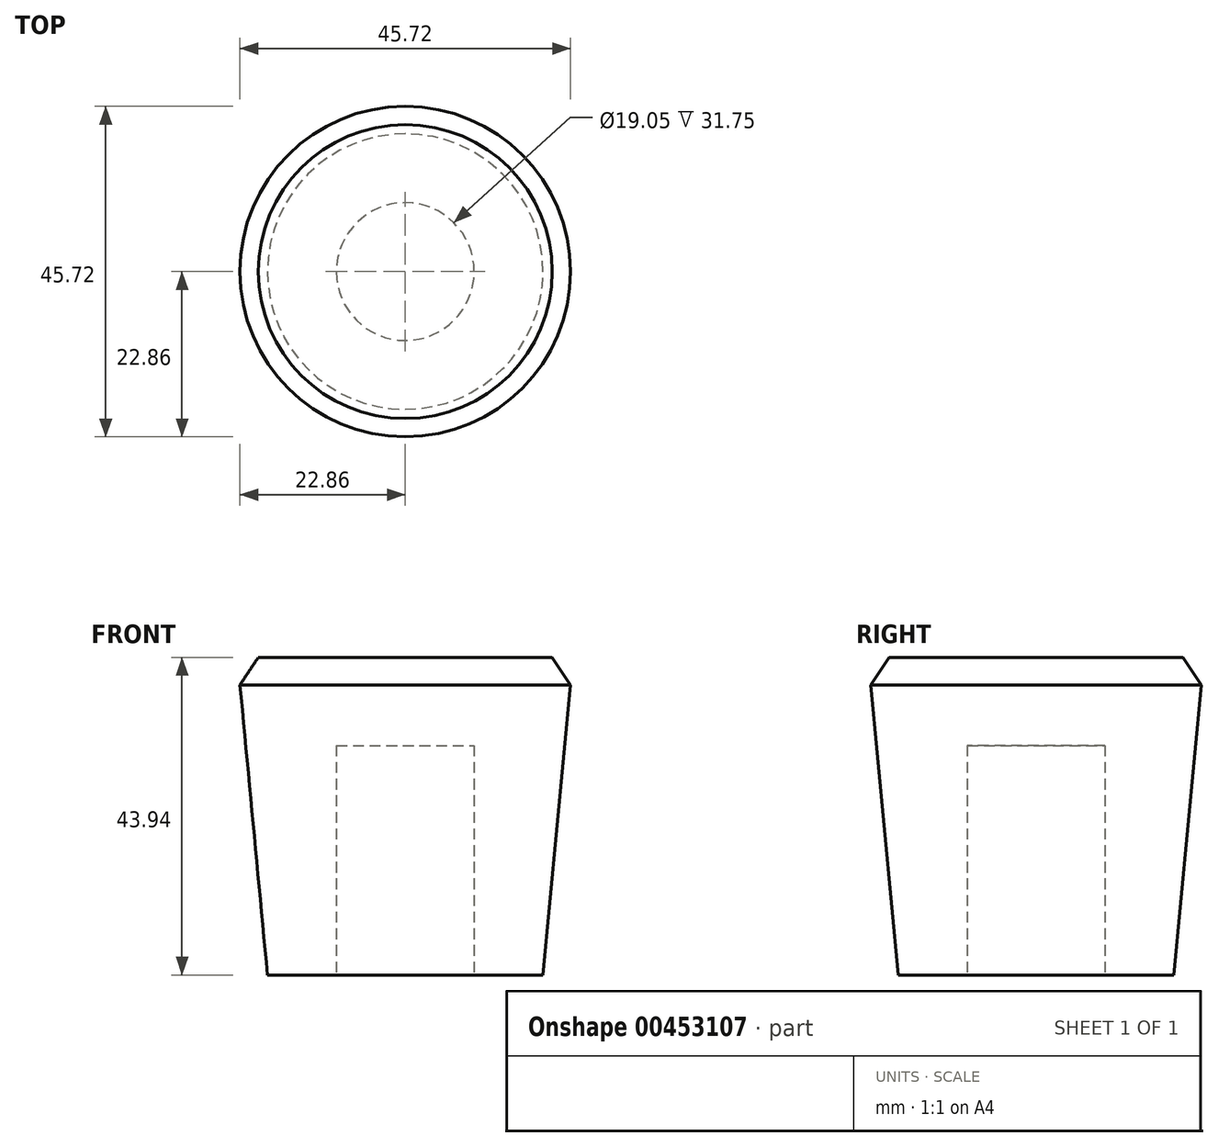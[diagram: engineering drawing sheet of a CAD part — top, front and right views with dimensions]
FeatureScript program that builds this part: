
annotation { "Feature Type Name" : "Feature", "Feature Type Description" : "" }
export const myFeature = defineFeature(function(context is Context, id is Id, definition is map)
    precondition{}
    {
        {
            var Q0;
            Q0=qCreatedBy(makeId("Front.planeOp"),FACE);
            var sketch = newSketch(context, id + "F0", { "sketchPlane" : qUnion([Q0])});
            skLineSegment(sketch, "E0", {"start": v(0, 36.16) * mm, "end": v(-20.32, 36.16) * mm});
            skLineSegment(sketch, "E1", {"start": v(-19.05, -7.78) * mm, "end": v(0, -7.78) * mm});
            skLineSegment(sketch, "E2", {"start": v(0, -7.78) * mm, "end": v(0, 36.16) * mm});
            skLineSegment(sketch, "E3", {"start": v(0, 32.35) * mm, "end": v(-58.87, 32.35) * mm, "construction": true});
            skLineSegment(sketch, "E4", {"start": v(-22.86, 56.9) * mm, "end": v(-22.86, -15.86) * mm, "construction": true});
            skLineSegment(sketch, "E5", {"start": v(-20.32, 36.16) * mm, "end": v(-22.86, 32.35) * mm});
            skLineSegment(sketch, "E6", {"start": v(-22.86, 32.35) * mm, "end": v(-19.05, -7.78) * mm});
            skSolve(sketch);
        }
        {
            var Q0;
            Q0 = qSketchRegion(id + "F0", true);
            var Q1;
            Q1=sQuery(id+"F0.wireOp",EDGE,"E2");
            revolve(context, id + "F1", {"entities" : qUnion([Q0]), "axis" : qUnion([Q1]), "revolveType" : RevolveType.FULL});
        }
        {
            var Q0;
            Q0=makeQuery(id+"F1.opRevolve","SWEPT_FACE",FACE,{"disambiguationData":[OSD([sQuery(id+"F0.wireOp",EDGE,"E1")])]});
            var sketch = newSketch(context, id + "F2", { "sketchPlane" : qUnion([Q0])});
            skCircle(sketch, "E7", {"center": v(0, 0) * mm, "radius": 9.53 * mm});
            skSolve(sketch);
        }
        {
            var Q0;
            Q0 = qSketchRegion(id + "F2", true);
            extrude(context, id + "F3", {"entities" : qUnion([Q0]), "operationType" : NewBodyOperationType.REMOVE, "oppositeDirection" : true, "depth" : 31.75 * mm});
        }
    });
